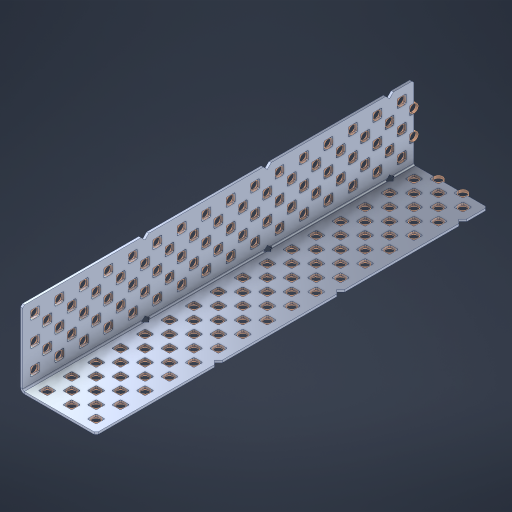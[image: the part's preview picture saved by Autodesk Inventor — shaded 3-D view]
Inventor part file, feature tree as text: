
AUTODESK INVENTOR PART (.ipt)
format: ipt  version: 2023 (Build 270158000, 158)  size: 1,855,488 bytes
history: native  units: in
note: dims shown in document units (in); Inventor stores cm internally (conversion verified against a paired STEP export)
features: other x166, extrude x158, sheet_metal_op x8, sketch x7, pattern_linear x3, mirror x1, chamfer x1
ambient origin geometry x8: Origin, YZ Plane, XZ Plane, XY Plane, X Axis, Y Axis, Z Axis, Center Point
bodies: Solid1 (feature_tree), Body (feature_tree)
feature tree (344):
  sheet_metal_op  "Flanges"
  sheet_metal_op  "Body Pattern"
  pattern_linear  "Center Double"  Spacing1=1.5in  [1 undecoded]
  pattern_linear  "Center Pattern"  Spacing1=0.1875in  [1 undecoded]
  other  "Arc Length"
  pattern_linear  "Notch Pattern"  Spacing1=0.0469in  [1 undecoded]
  other  "Diagonal Plane"
  mirror  "Everything Mirrored"
  chamfer  "End Chamfer"
  sketch  "Sketch1"  dims[d0=1.5in]
  other  "Plate1"
  sketch  "Sketch2"  dims[d1=8.0in]
  other  "Plate2"
  sheet_metal_op  "Bend1"
  sheet_metal_op  "Corner1"
  sketch  "Sketch8"  dims[d2=0.0469in]
  sketch  "Sketch9"  dims[d3=0.0469in]
  other  "Srf91"
  sheet_metal_op  "Body Pattern Sketch"
  other  "Srf92"
  sketch  "Sketch13"  dims[d4=0.0234in]
  sketch  "Sketch15"  dims[d5=0.0938in]
  sketch  "Sketch16"  dims[d6=0.0469in d7=1.5in d8=90.0deg d9=0.0312in d10=0.1875in d11=0.0469in d12=0.0469in d49=0.182in d50=0.02in d52=0.25in d53=0.0469in d54=0.0in d55=0.172in d56=1.0in d57=0.0in d85=0.1473in d86=0.1659in d89=0.0469in d90=0.0in d91=0.04in d92=0.0491in d95=2.5in d96=0.04in d97=0.25in d98=45.0deg d106=0.182in d107=0.02in d110=0.0469in d111=0.0in d112=0.172in d113=0.5in d114=0.0in d117=0.5in d126=0.0491in d127=0.1227in d128=0.08in d129=0.04in d130=2.5in d131=0.25in d132=6.2992in d134=0.5in d135=1.1811in d137=0.5in d140=0.5in d141=1.0in d142=0.3937in d144=0.5in d145=0.071in d146=0.7874in d148=0.5in]
  other  "Srf786"
  other  "Srf856"
  other  "Srf889"
  other  "Srf890"
  other  "Srf891"
  other  "Srf1275"
  other  "Srf1276"
  other  "Srf1278"
  other  "Srf1277"
  other  "Srf1285"
  other  "Srf1286"
  other  "Srf1287"
  other  "Srf1445"
  other  "Srf1446"
  other  "Srf1447"
  other  "Srf1448"
  other  "Srf1449"
  other  "Srf1537"
  other  "Srf1538"
  other  "Srf1539"
  other  "Srf1540"
  other  "Srf1541"
  other  "Srf1807"
  other  "Srf1808"
  other  "Srf1809"
  other  "Srf1810"
  other  "Srf1811"
  other  "Srf1812"
  other  "Srf1813"
  other  "Srf1959"
  other  "Srf1960"
  other  "Srf1961"
  other  "Srf1962"
  other  "Srf1963"
  other  "Srf1964"
  other  "Srf1965"
  other  "Srf2009"
  other  "Srf2010"
  other  "Srf2011"
  other  "Srf2012"
  other  "Srf2013"
  other  "Srf2014"
  other  "Srf2015"
  other  "Srf2016"
  other  "Srf2017"
  other  "Srf2018"
  other  "Srf2019"
  other  "Srf2020"
  other  "Srf2021"
  other  "Srf2022"
  other  "Srf2023"
  other  "Srf2024"
  other  "Srf2043"
  other  "Srf2044"
  other  "Srf2045"
  other  "Srf2046"
  other  "Srf2047"
  other  "Srf2048"
  other  "Srf2049"
  other  "Srf2050"
  other  "Srf2051"
  other  "Srf2052"
  other  "Srf2053"
  other  "Srf2054"
  other  "Srf2055"
  other  "Srf2056"
  other  "Srf2057"
  other  "Srf2076"
  other  "Srf2077"
  other  "Srf2078"
  other  "Srf2079"
  other  "Srf2080"
  other  "Srf2081"
  other  "Srf2082"
  other  "Srf2083"
  other  "Srf2084"
  other  "Srf2085"
  other  "Srf2086"
  other  "Srf2087"
  other  "Srf2088"
  other  "Srf2089"
  other  "Srf2090"
  other  "Srf2091"
  other  "Srf2092"
  other  "Srf2093"
  other  "Srf2094"
  other  "Srf2095"
  other  "Srf2096"
  other  "Srf2097"
  other  "Srf2098"
  other  "Srf2099"
  other  "Srf2100"
  other  "Srf2101"
  other  "Srf2102"
  other  "Srf2103"
  other  "Srf2104"
  other  "Srf2105"
  other  "Srf2106"
  other  "Srf2107"
  other  "Srf2108"
  other  "Srf2109"
  other  "Srf2110"
  other  "Srf2111"
  other  "Srf2112"
  other  "Srf2113"
  other  "Srf2114"
  other  "Srf2115"
  other  "Srf2116"
  other  "Srf2117"
  other  "Srf2118"
  other  "Srf2119"
  other  "Srf2120"
  other  "Srf2121"
  other  "Srf2179"
  other  "Srf2180"
  other  "Srf2181"
  other  "Srf2182"
  other  "Srf2183"
  other  "Srf2184"
  other  "Srf2185"
  other  "Srf2186"
  other  "Srf2187"
  other  "Srf2188"
  other  "Srf2189"
  other  "Srf2190"
  other  "Srf2191"
  other  "Srf2192"
  other  "Srf2193"
  other  "Srf2194"
  other  "Srf2195"
  other  "Srf2196"
  other  "Srf2197"
  other  "Srf2198"
  other  "Srf2199"
  other  "Srf2200"
  other  "Srf2201"
  other  "Srf2202"
  other  "Srf2203"
  other  "Srf2204"
  other  "Srf2205"
  other  "Srf2206"
  other  "Srf2207"
  other  "Srf2208"
  other  "Srf2209"
  other  "Srf2210"
  other  "Srf2211"
  other  "Srf2212"
  other  "Srf2213"
  other  "Srf2214"
  other  "Srf2215"
  other  "Srf2216"
  other  "Srf2217"
  other  "Srf2218"
  other  "Srf2219"
  other  "Srf2220"
  other  "Srf2221"
  other  "Srf2222"
  other  "Srf2223"
  sheet_metal_op  "Body Stamp"
  sheet_metal_op  "Body Circle"
  other  "Center Stamp"
  other  "Center Circle"
  sheet_metal_op  "Notch"
  extrude  "ExtrusionSrf92"  Depth=0.0469in
  extrude  "ExtrusionSrf856"  Depth=0.182in
  extrude  "ExtrusionSrf889"  Depth=0.02in
  extrude  "ExtrusionSrf890"  Depth=0.25in
  extrude  "ExtrusionSrf891"  Depth=0.0469in
  extrude  "ExtrusionSrf1275"  TaperAngle=0.0deg  [1 undecoded]
  extrude  "ExtrusionSrf1276"  Depth=0.5in
  extrude  "ExtrusionSrf1277"  Depth=1.0in TaperAngle=0.0deg
  extrude  "ExtrusionSrf1345"  Depth=0.5in
  extrude  "ExtrusionSrf1346"  Depth=0.5in
  extrude  "ExtrusionSrf1347"  Depth=0.0469in
  extrude  "ExtrusionSrf1348"  Depth=0.5in TaperAngle=0.0deg
  extrude  "ExtrusionSrf1445"  Depth=0.5in
  extrude  "ExtrusionSrf1446"  Depth=0.25in TaperAngle=45.0deg
  extrude  "ExtrusionSrf1447"  Depth=0.182in
  extrude  "ExtrusionSrf1448"  Depth=0.02in
  extrude  "ExtrusionSrf1449"  Depth=0.0469in
  extrude  "ExtrusionSrf1537"  TaperAngle=0.0deg  [1 undecoded]
  extrude  "ExtrusionSrf1538"  Depth=0.5in
  extrude  "ExtrusionSrf1539"  Depth=0.5in TaperAngle=0.0deg
  extrude  "ExtrusionSrf1540"  Depth=0.5in
  extrude  "ExtrusionSrf1541"  Depth=0.5in
  extrude  "ExtrusionSrf1807"  Depth=0.5in
  extrude  "ExtrusionSrf1808"  Depth=0.5in
  extrude  "ExtrusionSrf1809"  Depth=0.5in
  extrude  "ExtrusionSrf1810"  Depth=0.5in
  extrude  "ExtrusionSrf1811"  Depth=0.25in
  extrude  "ExtrusionSrf1812"  Depth=0.5in
  extrude  "ExtrusionSrf1813"  Depth=0.5in
  extrude  "ExtrusionSrf1959"  Depth=0.5in
  extrude  "ExtrusionSrf1960"  Depth=1.0in
  extrude  "ExtrusionSrf1961"  Depth=0.3937in
  extrude  "ExtrusionSrf1962"  Depth=0.5in
  extrude  "ExtrusionSrf1963"  Depth=0.5in
  extrude  "ExtrusionSrf1964"  [1 undecoded]
  extrude  "ExtrusionSrf1965"  [1 undecoded]
  extrude  "ExtrusionSrf2009"  [1 undecoded]
  extrude  "ExtrusionSrf2010"  [1 undecoded]
  extrude  "ExtrusionSrf2011"  [1 undecoded]
  extrude  "ExtrusionSrf2012"  [1 undecoded]
  extrude  "ExtrusionSrf2013"  [1 undecoded]
  extrude  "ExtrusionSrf2014"  [1 undecoded]
  extrude  "ExtrusionSrf2015"  [1 undecoded]
  extrude  "ExtrusionSrf2016"  [1 undecoded]
  extrude  "ExtrusionSrf2017"  [1 undecoded]
  extrude  "ExtrusionSrf2018"  [1 undecoded]
  extrude  "ExtrusionSrf2019"  [1 undecoded]
  extrude  "ExtrusionSrf2020"  [1 undecoded]
  extrude  "ExtrusionSrf2021"  [1 undecoded]
  extrude  "ExtrusionSrf2022"  [1 undecoded]
  extrude  "ExtrusionSrf2023"  [1 undecoded]
  extrude  "ExtrusionSrf2024"  [1 undecoded]
  extrude  "ExtrusionSrf2043"  [1 undecoded]
  extrude  "ExtrusionSrf2044"  [1 undecoded]
  extrude  "ExtrusionSrf2045"  [1 undecoded]
  extrude  "ExtrusionSrf2046"  [1 undecoded]
  extrude  "ExtrusionSrf2047"  [1 undecoded]
  extrude  "ExtrusionSrf2048"  [1 undecoded]
  extrude  "ExtrusionSrf2049"  [1 undecoded]
  extrude  "ExtrusionSrf2050"  [1 undecoded]
  extrude  "ExtrusionSrf2051"  [1 undecoded]
  extrude  "ExtrusionSrf2052"  [1 undecoded]
  extrude  "ExtrusionSrf2053"  [1 undecoded]
  extrude  "ExtrusionSrf2054"  [1 undecoded]
  extrude  "ExtrusionSrf2055"  [1 undecoded]
  extrude  "ExtrusionSrf2056"  [1 undecoded]
  extrude  "ExtrusionSrf2057"  [1 undecoded]
  extrude  "ExtrusionSrf2076"  [1 undecoded]
  extrude  "ExtrusionSrf2077"  [1 undecoded]
  extrude  "ExtrusionSrf2078"  [1 undecoded]
  extrude  "ExtrusionSrf2079"  [1 undecoded]
  extrude  "ExtrusionSrf2080"  [1 undecoded]
  extrude  "ExtrusionSrf2081"  [1 undecoded]
  extrude  "ExtrusionSrf2082"  [1 undecoded]
  extrude  "ExtrusionSrf2083"  [1 undecoded]
  extrude  "ExtrusionSrf2084"  [1 undecoded]
  extrude  "ExtrusionSrf2085"  [1 undecoded]
  extrude  "ExtrusionSrf2086"  [1 undecoded]
  extrude  "ExtrusionSrf2087"  [1 undecoded]
  extrude  "ExtrusionSrf2088"  [1 undecoded]
  extrude  "ExtrusionSrf2089"  [1 undecoded]
  extrude  "ExtrusionSrf2090"  [1 undecoded]
  extrude  "ExtrusionSrf2091"  [1 undecoded]
  extrude  "ExtrusionSrf2092"  [1 undecoded]
  extrude  "ExtrusionSrf2093"  [1 undecoded]
  extrude  "ExtrusionSrf2094"  [1 undecoded]
  extrude  "ExtrusionSrf2095"  [1 undecoded]
  extrude  "ExtrusionSrf2096"  [1 undecoded]
  extrude  "ExtrusionSrf2097"  [1 undecoded]
  extrude  "ExtrusionSrf2098"  [1 undecoded]
  extrude  "ExtrusionSrf2099"  [1 undecoded]
  extrude  "ExtrusionSrf2100"  [1 undecoded]
  extrude  "ExtrusionSrf2101"  [1 undecoded]
  extrude  "ExtrusionSrf2102"  [1 undecoded]
  extrude  "ExtrusionSrf2103"  [1 undecoded]
  extrude  "ExtrusionSrf2104"  [1 undecoded]
  extrude  "ExtrusionSrf2105"  [1 undecoded]
  extrude  "ExtrusionSrf2106"  [1 undecoded]
  extrude  "ExtrusionSrf2107"  [1 undecoded]
  extrude  "ExtrusionSrf2108"  [1 undecoded]
  extrude  "ExtrusionSrf2109"  [1 undecoded]
  extrude  "ExtrusionSrf2110"  [1 undecoded]
  extrude  "ExtrusionSrf2111"  [1 undecoded]
  extrude  "ExtrusionSrf2112"  [1 undecoded]
  extrude  "ExtrusionSrf2113"  [1 undecoded]
  extrude  "ExtrusionSrf2114"  [1 undecoded]
  extrude  "ExtrusionSrf2115"  [1 undecoded]
  extrude  "ExtrusionSrf2116"  [1 undecoded]
  extrude  "ExtrusionSrf2117"  [1 undecoded]
  extrude  "ExtrusionSrf2118"  [1 undecoded]
  extrude  "ExtrusionSrf2119"  [1 undecoded]
  extrude  "ExtrusionSrf2120"  [1 undecoded]
  extrude  "ExtrusionSrf2121"  [1 undecoded]
  extrude  "ExtrusionSrf2179"  [1 undecoded]
  extrude  "ExtrusionSrf2180"  [1 undecoded]
  extrude  "ExtrusionSrf2181"  [1 undecoded]
  extrude  "ExtrusionSrf2182"  [1 undecoded]
  extrude  "ExtrusionSrf2183"  [1 undecoded]
  extrude  "ExtrusionSrf2184"  [1 undecoded]
  extrude  "ExtrusionSrf2185"  [1 undecoded]
  extrude  "ExtrusionSrf2186"  [1 undecoded]
  extrude  "ExtrusionSrf2187"  [1 undecoded]
  extrude  "ExtrusionSrf2188"  [1 undecoded]
  extrude  "ExtrusionSrf2189"  [1 undecoded]
  extrude  "ExtrusionSrf2190"  [1 undecoded]
  extrude  "ExtrusionSrf2191"  [1 undecoded]
  extrude  "ExtrusionSrf2192"  [1 undecoded]
  extrude  "ExtrusionSrf2193"  [1 undecoded]
  extrude  "ExtrusionSrf2194"  [1 undecoded]
  extrude  "ExtrusionSrf2195"  [1 undecoded]
  extrude  "ExtrusionSrf2196"  [1 undecoded]
  extrude  "ExtrusionSrf2197"  [1 undecoded]
  extrude  "ExtrusionSrf2198"  [1 undecoded]
  extrude  "ExtrusionSrf2199"  [1 undecoded]
  extrude  "ExtrusionSrf2200"  [1 undecoded]
  extrude  "ExtrusionSrf2201"  [1 undecoded]
  extrude  "ExtrusionSrf2202"  [1 undecoded]
  extrude  "ExtrusionSrf2203"  [1 undecoded]
  extrude  "ExtrusionSrf2204"  [1 undecoded]
  extrude  "ExtrusionSrf2205"  [1 undecoded]
  extrude  "ExtrusionSrf2206"  [1 undecoded]
  extrude  "ExtrusionSrf2207"  [1 undecoded]
  extrude  "ExtrusionSrf2208"  [1 undecoded]
  extrude  "ExtrusionSrf2209"  [1 undecoded]
  extrude  "ExtrusionSrf2210"  [1 undecoded]
  extrude  "ExtrusionSrf2211"  [1 undecoded]
  extrude  "ExtrusionSrf2212"  [1 undecoded]
  extrude  "ExtrusionSrf2213"  [1 undecoded]
  extrude  "ExtrusionSrf2214"  [1 undecoded]
  extrude  "ExtrusionSrf2215"  [1 undecoded]
  extrude  "ExtrusionSrf2216"  [1 undecoded]
  extrude  "ExtrusionSrf2217"  [1 undecoded]
  extrude  "ExtrusionSrf2218"  [1 undecoded]
  extrude  "ExtrusionSrf2219"  [1 undecoded]
  extrude  "ExtrusionSrf2220"  [1 undecoded]
  extrude  "ExtrusionSrf2221"  [1 undecoded]
  extrude  "ExtrusionSrf2222"  [1 undecoded]
  extrude  "ExtrusionSrf2223"  [1 undecoded]
note: 129 required parameter values undecoded (feature->parameter linkage not recoverable at this tier; creation-order binding heuristic only, values carry confidence <= 0.55)
